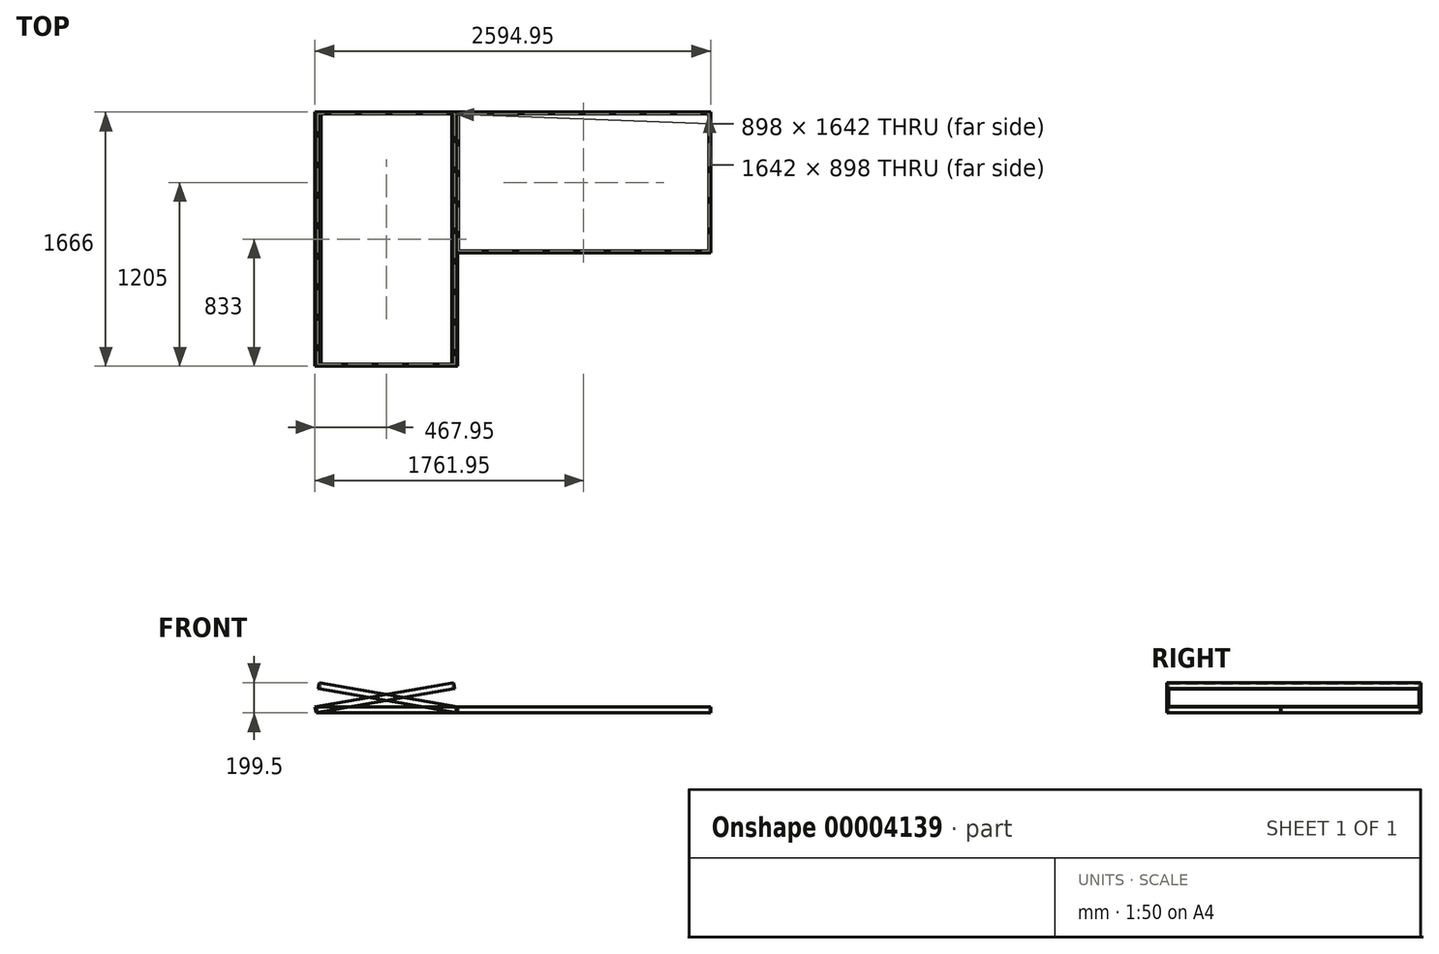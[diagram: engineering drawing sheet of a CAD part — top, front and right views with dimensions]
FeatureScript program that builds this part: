
annotation { "Feature Type Name" : "Feature", "Feature Type Description" : "" }
export const myFeature = defineFeature(function(context is Context, id is Id, definition is map)
    precondition{}
    {
        {
            var Q0;
            Q0=qCreatedBy(makeId("Top.planeOp"),FACE);
            var sketch = newSketch(context, id + "F0", { "sketchPlane" : qUnion([Q0])});
            skLineSegment(sketch, "E0.rect.bottom", {"start": v(833, -461) * mm, "end": v(-833, -461) * mm});
            skLineSegment(sketch, "E0.rect.top", {"start": v(833, 461) * mm, "end": v(-833, 461) * mm});
            skLineSegment(sketch, "E0.rect.left", {"start": v(833, -461) * mm, "end": v(833, 461) * mm});
            skLineSegment(sketch, "E0.rect.right", {"start": v(-833, -461) * mm, "end": v(-833, 461) * mm});
            skPoint(sketch, "E0.rect.middle", {"position": v(0, 0) * mm});
            skLineSegment(sketch, "E1.rect.bottom", {"start": v(821, -449) * mm, "end": v(-821, -449) * mm});
            skLineSegment(sketch, "E1.rect.top", {"start": v(821, 449) * mm, "end": v(-821, 449) * mm});
            skLineSegment(sketch, "E1.rect.left", {"start": v(821, -449) * mm, "end": v(821, 449) * mm});
            skLineSegment(sketch, "E1.rect.right", {"start": v(-821, -449) * mm, "end": v(-821, 449) * mm});
            skSolve(sketch);
        }
        {
            var Q0;
            Q0=makeQuery(id+"F0.imprint","IMPRINT",FACE,{"disambiguationData":[TD([[makeQuery(id+"F0.imprint","IMPRINT",EDGE,{"derivedFrom":sQuery(id+"F0.wireOp",EDGE,"E0.rect.bottom")}),-1.0]])]});
            extrude(context, id + "F1", {"entities" : qUnion([Q0]), "depth" : 40 * mm});
        }
        {
            var Q0;
            Q0=qCreatedBy(makeId("Top.planeOp"),FACE);
            var sketch = newSketch(context, id + "F2", { "sketchPlane" : qUnion([Q0])});
            skLineSegment(sketch, "E2.rect.bottom", {"start": v(821, 449) * mm, "end": v(-821, 449) * mm});
            skLineSegment(sketch, "E2.rect.top", {"start": v(821, -449) * mm, "end": v(-821, -449) * mm});
            skLineSegment(sketch, "E2.rect.left", {"start": v(821, 449) * mm, "end": v(821, -449) * mm});
            skLineSegment(sketch, "E2.rect.right", {"start": v(-821, 449) * mm, "end": v(-821, -449) * mm});
            skPoint(sketch, "E2.rect.middle", {"position": v(0, 0) * mm});
            skSolve(sketch);
        }
        {
            var Q0;
            Q0=makeQuery(id+"F2.imprint","IMPRINT",FACE,{"disambiguationData":[TD([[makeQuery(id+"F2.imprint","IMPRINT",EDGE,{"derivedFrom":sQuery(id+"F2.wireOp",EDGE,"E2.rect.bottom")}),1.0]])]});
            extrude(context, id + "F3", {"entities" : qUnion([Q0]), "depth" : 38 * mm});
        }
        {
            var Q0;
            Q0=makeQuery(id+"F3.opExtrude","CAP_FACE",FACE,{"disambiguationData":[OSD([sQuery(id+"F2.wireOp",EDGE,"E2.rect.bottom"),sQuery(id+"F2.wireOp",EDGE,"E2.rect.top"),sQuery(id+"F2.wireOp",EDGE,"E2.rect.left"),sQuery(id+"F2.wireOp",EDGE,"E2.rect.right")])],"isStart":true});
            extrude(context, id + "F4", {"entities" : qUnion([Q0]), "operationType" : NewBodyOperationType.REMOVE, "oppositeDirection" : true, "depth" : 36 * mm});
        }
        {
            var Q0;
            Q0=makeQuery(id+"F1.opExtrude","SWEPT_BODY",BODY,{"disambiguationData":[OSD([sQuery(id+"F0.wireOp",EDGE,"E0.rect.bottom"),sQuery(id+"F0.wireOp",EDGE,"E0.rect.top"),sQuery(id+"F0.wireOp",EDGE,"E0.rect.left"),sQuery(id+"F0.wireOp",EDGE,"E0.rect.right"),sQuery(id+"F0.wireOp",EDGE,"E1.rect.bottom"),sQuery(id+"F0.wireOp",EDGE,"E1.rect.top"),sQuery(id+"F0.wireOp",EDGE,"E1.rect.left"),sQuery(id+"F0.wireOp",EDGE,"E1.rect.right")])]});
            var Q1;
            Q1=makeQuery(id+"F3.opExtrude","SWEPT_BODY",BODY,{"disambiguationData":[OSD([sQuery(id+"F2.wireOp",EDGE,"E2.rect.bottom"),sQuery(id+"F2.wireOp",EDGE,"E2.rect.top"),sQuery(id+"F2.wireOp",EDGE,"E2.rect.left"),sQuery(id+"F2.wireOp",EDGE,"E2.rect.right")])]});
            var Q2;
            Q2=makeQuery(id+"F1.opExtrude","SWEPT_EDGE",EDGE,{"disambiguationData":[OSD([sQuery(id+"F0.wireOp",EDGE,"E0.rect.top"),sQuery(id+"F0.wireOp",EDGE,"E0.rect.right")])]});
            transform(context, id + "F5", {"entities" : qUnion([Q0, Q1]), "transformType" : TransformType.ROTATION, "transformAxis" : qUnion([Q2]), "angle" : 90 * degree, "makeCopy" : true});
        }
        {
            var Q0;
            Q0=makeQuery(id+"F5.opPattern","COPY",BODY,{"derivedFrom":makeQuery(id+"F1.opExtrude","SWEPT_BODY",BODY,{"disambiguationData":[OSD([sQuery(id+"F0.wireOp",EDGE,"E0.rect.bottom"),sQuery(id+"F0.wireOp",EDGE,"E0.rect.top"),sQuery(id+"F0.wireOp",EDGE,"E0.rect.left"),sQuery(id+"F0.wireOp",EDGE,"E0.rect.right"),sQuery(id+"F0.wireOp",EDGE,"E1.rect.bottom"),sQuery(id+"F0.wireOp",EDGE,"E1.rect.top"),sQuery(id+"F0.wireOp",EDGE,"E1.rect.left"),sQuery(id+"F0.wireOp",EDGE,"E1.rect.right")])]}),"instanceName":"1"});
            var Q1;
            Q1=makeQuery(id+"F5.opPattern","COPY",BODY,{"derivedFrom":makeQuery(id+"F3.opExtrude","SWEPT_BODY",BODY,{"disambiguationData":[OSD([sQuery(id+"F2.wireOp",EDGE,"E2.rect.bottom"),sQuery(id+"F2.wireOp",EDGE,"E2.rect.top"),sQuery(id+"F2.wireOp",EDGE,"E2.rect.left"),sQuery(id+"F2.wireOp",EDGE,"E2.rect.right")])]}),"instanceName":"1"});
            var Q2;
            Q2=makeQuery(id+"F5.opPattern","COPY",EDGE,{"derivedFrom":makeQuery(id+"F1.opExtrude","CAP_EDGE",EDGE,{"disambiguationData":[OSD([sQuery(id+"F0.wireOp",EDGE,"E0.rect.bottom")])],"isStart":true}),"instanceName":"1"});
            transform(context, id + "F6", {"entities" : qUnion([Q0, Q1]), "transformType" : TransformType.ROTATION, "transformAxis" : qUnion([Q2]), "angle" : 10 * degree, "oppositeDirection" : true, "makeCopy" : true});
        }
        {
            var Q0;
            Q0=makeQuery(id+"F5.opPattern","COPY",BODY,{"derivedFrom":makeQuery(id+"F3.opExtrude","SWEPT_BODY",BODY,{"disambiguationData":[OSD([sQuery(id+"F2.wireOp",EDGE,"E2.rect.bottom"),sQuery(id+"F2.wireOp",EDGE,"E2.rect.top"),sQuery(id+"F2.wireOp",EDGE,"E2.rect.left"),sQuery(id+"F2.wireOp",EDGE,"E2.rect.right")])]}),"instanceName":"1"});
            var Q1;
            Q1=makeQuery(id+"F5.opPattern","COPY",BODY,{"derivedFrom":makeQuery(id+"F1.opExtrude","SWEPT_BODY",BODY,{"disambiguationData":[OSD([sQuery(id+"F0.wireOp",EDGE,"E0.rect.bottom"),sQuery(id+"F0.wireOp",EDGE,"E0.rect.top"),sQuery(id+"F0.wireOp",EDGE,"E0.rect.left"),sQuery(id+"F0.wireOp",EDGE,"E0.rect.right"),sQuery(id+"F0.wireOp",EDGE,"E1.rect.bottom"),sQuery(id+"F0.wireOp",EDGE,"E1.rect.top"),sQuery(id+"F0.wireOp",EDGE,"E1.rect.left"),sQuery(id+"F0.wireOp",EDGE,"E1.rect.right")])]}),"instanceName":"1"});
            var Q2;
            Q2=makeQuery(id+"F5.opPattern","COPY",EDGE,{"derivedFrom":makeQuery(id+"F1.opExtrude","CAP_EDGE",EDGE,{"disambiguationData":[OSD([sQuery(id+"F0.wireOp",EDGE,"E0.rect.top")])],"isStart":true}),"instanceName":"1"});
            transform(context, id + "F7", {"entities" : qUnion([Q0, Q1]), "transformType" : TransformType.ROTATION, "transformAxis" : qUnion([Q2]), "angle" : 10 * degree, "makeCopy" : true});
        }
    });
